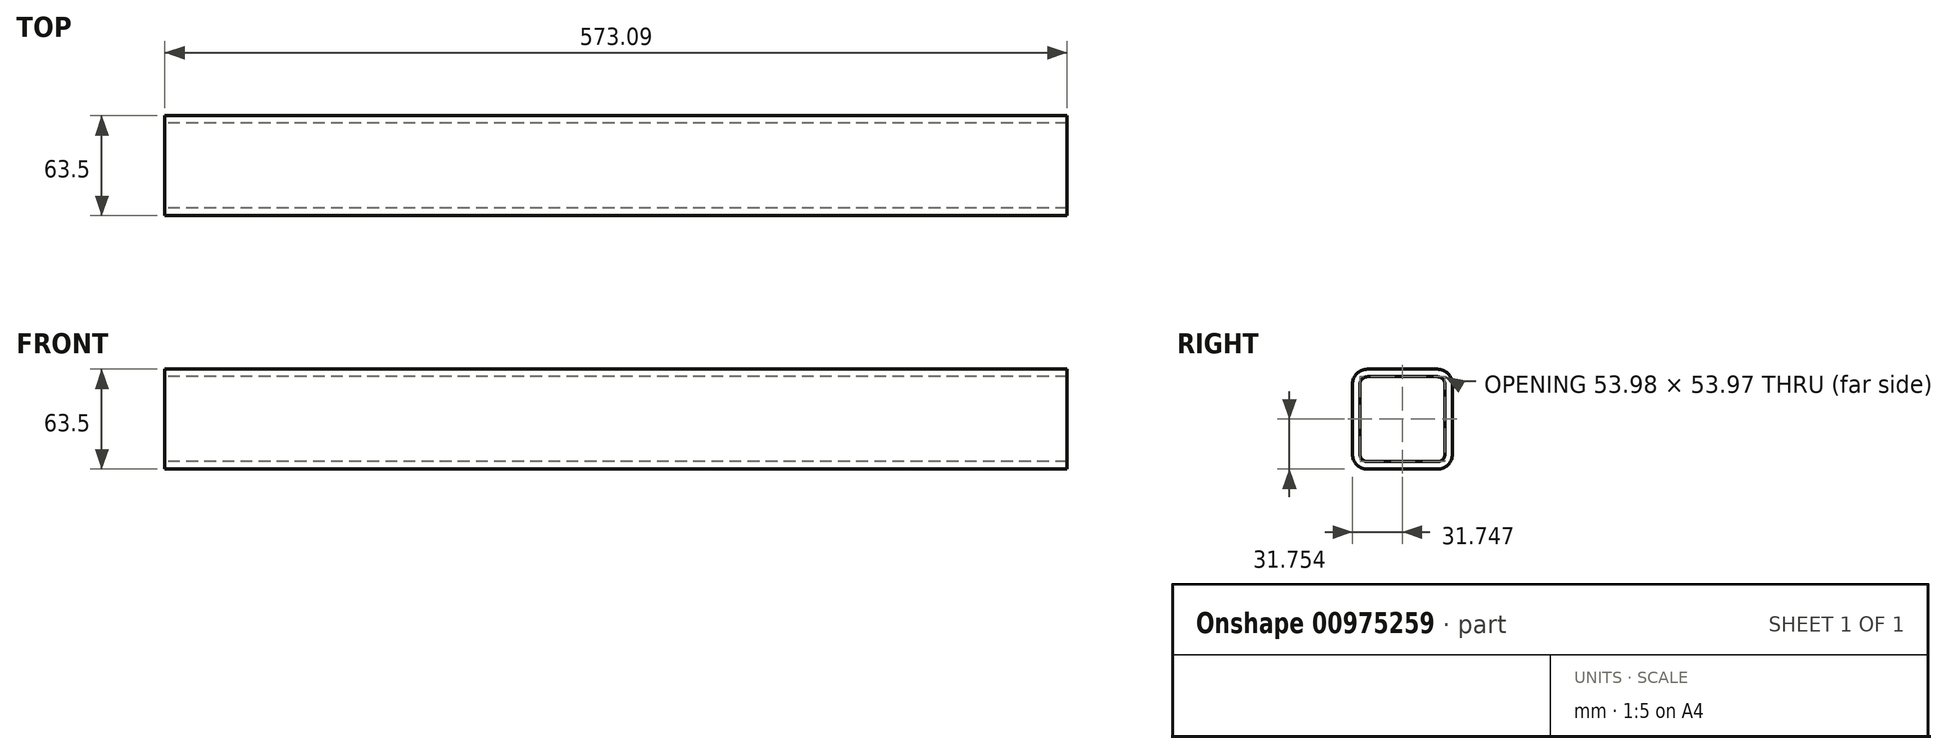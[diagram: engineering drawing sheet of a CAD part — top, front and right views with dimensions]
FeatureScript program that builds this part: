
annotation { "Feature Type Name" : "Feature", "Feature Type Description" : "" }
export const myFeature = defineFeature(function(context is Context, id is Id, definition is map)
    precondition{}
    {
        {
            var Q0;
            Q0=qCreatedBy(makeId("Right.planeOp"),FACE);
            var sketch = newSketch(context, id + "F0", { "sketchPlane" : qUnion([Q0])});
            skLineSegment(sketch, "E0.0", {"start": v(-5.77, 47.25) * mm, "end": v(38.68, 47.25) * mm});
            skLineSegment(sketch, "E0.1", {"start": v(-10.53, -1.96) * mm, "end": v(-10.53, 42.49) * mm});
            skLineSegment(sketch, "E0.2", {"start": v(-5.77, -6.72) * mm, "end": v(38.68, -6.72) * mm});
            skLineSegment(sketch, "E0.3", {"start": v(43.44, -1.96) * mm, "end": v(43.44, 42.49) * mm});
            skArc(sketch, "E1.filletArc", {"start": v(43.44, 42.49) * mm, "mid": v(42.05, 45.86) * mm, "end": v(38.68, 47.25) * mm});
            skPoint(sketch, "E2.visualSharp", {"position": v(43.44, -6.72) * mm});
            skArc(sketch, "E2.filletArc", {"start": v(38.68, -6.72) * mm, "mid": v(42.05, -5.33) * mm, "end": v(43.44, -1.96) * mm});
            skPoint(sketch, "E3.visualSharp", {"position": v(-10.53, -6.72) * mm});
            skArc(sketch, "E3.filletArc", {"start": v(-10.53, -1.96) * mm, "mid": v(-9.14, -5.33) * mm, "end": v(-5.77, -6.72) * mm});
            skArc(sketch, "E4.filletArc", {"start": v(-5.77, 47.25) * mm, "mid": v(-9.14, 45.86) * mm, "end": v(-10.53, 42.49) * mm});
            skLineSegment(sketch, "E5.0", {"start": v(48.2, -1.96) * mm, "end": v(48.2, 42.49) * mm});
            skArc(sketch, "E5.1", {"start": v(38.68, -11.49) * mm, "mid": v(45.42, -8.7) * mm, "end": v(48.2, -1.96) * mm});
            skArc(sketch, "E5.2", {"start": v(48.2, 42.49) * mm, "mid": v(45.42, 49.22) * mm, "end": v(38.68, 52.01) * mm});
            skLineSegment(sketch, "E5.3", {"start": v(-5.77, -11.49) * mm, "end": v(38.68, -11.49) * mm});
            skLineSegment(sketch, "E5.4", {"start": v(-5.77, 52.01) * mm, "end": v(38.68, 52.01) * mm});
            skArc(sketch, "E5.5", {"start": v(-5.77, 52.01) * mm, "mid": v(-12.5, 49.22) * mm, "end": v(-15.3, 42.49) * mm});
            skLineSegment(sketch, "E5.6", {"start": v(-15.3, -1.96) * mm, "end": v(-15.3, 42.49) * mm});
            skArc(sketch, "E5.7", {"start": v(-15.3, -1.96) * mm, "mid": v(-12.5, -8.7) * mm, "end": v(-5.77, -11.49) * mm});
            skSolve(sketch);
        }
        {
            var Q0;
            Q0=makeQuery(id+"F0.imprint","IMPRINT",FACE,{"disambiguationData":[TD([[makeQuery(id+"F0.imprint","IMPRINT",EDGE,{"derivedFrom":sQuery(id+"F0.wireOp",EDGE,"E0.0")}),1.0]])]});
            extrude(context, id + "F1", {"entities" : qUnion([Q0]), "depth" : 573.1 * mm, "offsetDistance" : 25.4 * mm});
        }
    });
